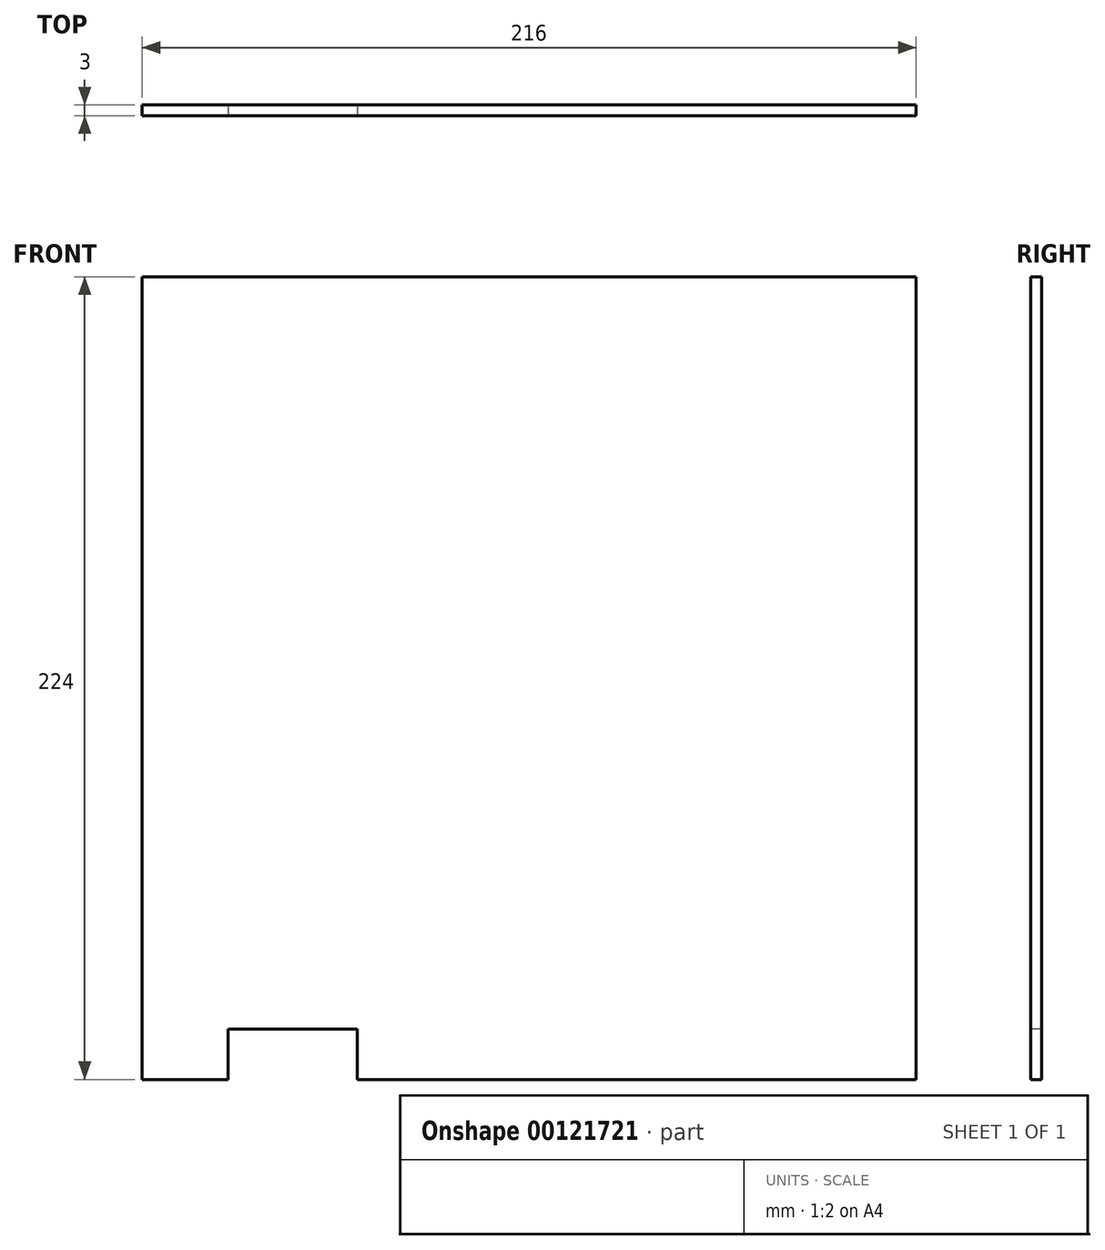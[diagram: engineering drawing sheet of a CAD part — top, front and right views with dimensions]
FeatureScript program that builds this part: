
annotation { "Feature Type Name" : "Feature", "Feature Type Description" : "" }
export const myFeature = defineFeature(function(context is Context, id is Id, definition is map)
    precondition{}
    {
        {
            var Q0;
            Q0=qCreatedBy(makeId("Front.planeOp"),FACE);
            var sketch = newSketch(context, id + "F0", { "sketchPlane" : qUnion([Q0])});
            skLineSegment(sketch, "E0.bottom", {"start": v(0, 0) * mm, "end": v(216, 0) * mm});
            skLineSegment(sketch, "E0.top", {"start": v(0, 224) * mm, "end": v(216, 224) * mm});
            skLineSegment(sketch, "E0.left", {"start": v(0, 0) * mm, "end": v(0, 224) * mm});
            skLineSegment(sketch, "E0.right", {"start": v(216, 0) * mm, "end": v(216, 224) * mm});
            skSolve(sketch);
        }
        {
            var Q0;
            Q0=qSketchRegion(id+"F0",true);
            var Q1;
            Q1=makeQuery(id+"F0.imprint","IMPRINT",FACE,{"disambiguationData":[TD([[makeQuery(id+"F0.imprint","IMPRINT",EDGE,{"derivedFrom":sQuery(id+"F0.wireOp",EDGE,"E0.bottom")}),1.0]])]});
            extrude(context, id + "F1", {"entities" : qUnion([Q0, Q1]), "depth" : 3 * mm});
        }
        {
            var Q0;
            Q0=makeQuery(id+"F1.opExtrude","CAP_FACE",FACE,{"disambiguationData":[OSD([sQuery(id+"F0.wireOp",EDGE,"E0.bottom"),sQuery(id+"F0.wireOp",EDGE,"E0.top"),sQuery(id+"F0.wireOp",EDGE,"E0.left"),sQuery(id+"F0.wireOp",EDGE,"E0.right")])],"isStart":false});
            var sketch = newSketch(context, id + "F2", { "sketchPlane" : qUnion([Q0])});
            skLineSegment(sketch, "E1.bottom", {"start": v(24, 0) * mm, "end": v(60, 0) * mm});
            skLineSegment(sketch, "E1.top", {"start": v(24, 14) * mm, "end": v(60, 14) * mm});
            skLineSegment(sketch, "E1.left", {"start": v(24, 0) * mm, "end": v(24, 14) * mm});
            skLineSegment(sketch, "E1.right", {"start": v(60, 0) * mm, "end": v(60, 14) * mm});
            skSolve(sketch);
        }
        {
            var Q0;
            Q0=makeQuery(id+"F2.imprint","IMPRINT",FACE,{"disambiguationData":[TD([[makeQuery(id+"F2.imprint","IMPRINT",EDGE,{"derivedFrom":sQuery(id+"F2.wireOp",EDGE,"E1.bottom")}),1.0]])]});
            extrude(context, id + "F3", {"entities" : qUnion([Q0]), "operationType" : NewBodyOperationType.REMOVE, "endBound" : BoundingType.THROUGH_ALL, "oppositeDirection" : true, "depth" : 25 * mm});
        }
    });
